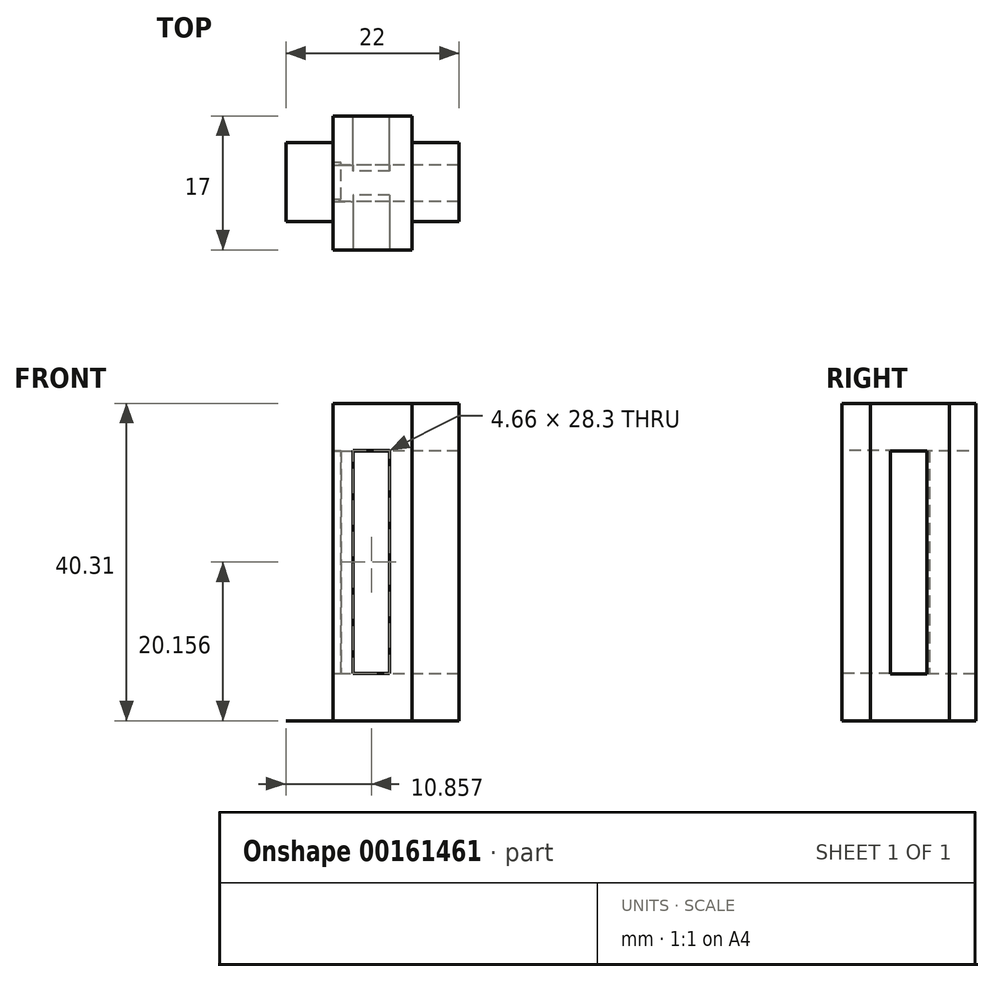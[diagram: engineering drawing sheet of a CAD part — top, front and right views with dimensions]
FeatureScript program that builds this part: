
annotation { "Feature Type Name" : "Feature", "Feature Type Description" : "" }
export const myFeature = defineFeature(function(context is Context, id is Id, definition is map)
    precondition{}
    {
        {
            var Q0;
            Q0=qCreatedBy(makeId("Front.planeOp"),FACE);
            var sketch = newSketch(context, id + "F0", { "sketchPlane" : qUnion([Q0])});
            skLineSegment(sketch, "E0.bottom", {"start": v(-30.25, -40.58) * mm, "end": v(-20.25, -40.58) * mm});
            skLineSegment(sketch, "E0.top", {"start": v(-30.25, -80.88) * mm, "end": v(-20.25, -80.88) * mm});
            skLineSegment(sketch, "E0.left", {"start": v(-30.25, -40.58) * mm, "end": v(-30.25, -80.88) * mm});
            skLineSegment(sketch, "E0.right", {"start": v(-20.25, -40.58) * mm, "end": v(-20.25, -80.88) * mm});
            skLineSegment(sketch, "E1.bottom", {"start": v(-23.06, -46.58) * mm, "end": v(-27.72, -46.58) * mm});
            skLineSegment(sketch, "E1.top", {"start": v(-23.06, -74.88) * mm, "end": v(-27.72, -74.88) * mm});
            skLineSegment(sketch, "E1.left", {"start": v(-23.06, -46.58) * mm, "end": v(-23.06, -74.88) * mm});
            skLineSegment(sketch, "E1.right", {"start": v(-27.72, -46.58) * mm, "end": v(-27.72, -74.88) * mm});
            skLineSegment(sketch, "E2", {"start": v(-23.06, -74.88) * mm, "end": v(-23.06, -80.88) * mm, "construction": true});
            skLineSegment(sketch, "E3", {"start": v(-27.72, -46.58) * mm, "end": v(-27.72, -40.58) * mm, "construction": true});
            skSolve(sketch);
        }
        {
            var Q0;
            Q0=makeQuery(id+"F0.imprint","IMPRINT",FACE,{"disambiguationData":[TD([[makeQuery(id+"F0.imprint","IMPRINT",EDGE,{"derivedFrom":sQuery(id+"F0.wireOp",EDGE,"E0.bottom")}),-1.0]])]});
            var Q1;
            Q1=makeQuery(id+"F0.imprint","IMPRINT",FACE,{"disambiguationData":[TD([[makeQuery(id+"F0.imprint","IMPRINT",EDGE,{"derivedFrom":sQuery(id+"F0.wireOp",EDGE,"0H4b4fvO-dyxi-FZrW-pJNc-f5h2Ua2qFgm1.bottom")}),-1.0]])]});
            var Q2;
            Q2=makeQuery(id+"F0.imprint","IMPRINT",FACE,{"disambiguationData":[TD([[makeQuery(id+"F0.imprint","IMPRINT",EDGE,{"derivedFrom":sQuery(id+"F0.wireOp",EDGE,"RIwqPRcQ-8Yhb-SA2c-7hZh-BoyqNhFDoh6P.bottom")}),-1.0]])]});
            var Q3;
            Q3=makeQuery(id+"F0.imprint","IMPRINT",FACE,{"disambiguationData":[TD([[makeQuery(id+"F0.imprint","IMPRINT",EDGE,{"derivedFrom":sQuery(id+"F0.wireOp",EDGE,"V1CP0RN2-3pWF-4ICx-AOtc-XG8nw0NRMOAc.bottom")}),-1.0]])]});
            var Q4;
            Q4=makeQuery(id+"F0.imprint","IMPRINT",FACE,{"disambiguationData":[TD([[makeQuery(id+"F0.imprint","IMPRINT",EDGE,{"derivedFrom":sQuery(id+"F0.wireOp",EDGE,"E1.bottom")}),1.0]])]});
            extrude(context, id + "F1", {"entities" : qUnion([Q0, Q1, Q2, Q3, Q4]), "depth" : 8.5 * mm});
        }
        {
            var Q0;
            Q0=makeQuery(id+"F0.imprint","IMPRINT",FACE,{"disambiguationData":[TD([[makeQuery(id+"F0.imprint","IMPRINT",EDGE,{"derivedFrom":sQuery(id+"F0.wireOp",EDGE,"0H4b4fvO-dyxi-FZrW-pJNc-f5h2Ua2qFgm1.bottom")}),-1.0]])]});
            var Q1;
            Q1=makeQuery(id+"F0.imprint","IMPRINT",FACE,{"disambiguationData":[TD([[makeQuery(id+"F0.imprint","IMPRINT",EDGE,{"derivedFrom":sQuery(id+"F0.wireOp",EDGE,"RIwqPRcQ-8Yhb-SA2c-7hZh-BoyqNhFDoh6P.bottom")}),-1.0]])]});
            var Q2;
            Q2=makeQuery(id+"F0.imprint","IMPRINT",FACE,{"disambiguationData":[TD([[makeQuery(id+"F0.imprint","IMPRINT",EDGE,{"derivedFrom":sQuery(id+"F0.wireOp",EDGE,"V1CP0RN2-3pWF-4ICx-AOtc-XG8nw0NRMOAc.bottom")}),-1.0]])]});
            var Q3;
            Q3=makeQuery(id+"F0.imprint","IMPRINT",FACE,{"disambiguationData":[TD([[makeQuery(id+"F0.imprint","IMPRINT",EDGE,{"derivedFrom":sQuery(id+"F0.wireOp",EDGE,"E1.bottom")}),1.0]])]});
            extrude(context, id + "F2", {"entities" : qUnion([Q0, Q1, Q2, Q3]), "operationType" : NewBodyOperationType.REMOVE, "depth" : 7 * mm});
        }
        {
            var Q0;
            Q0=makeQuery(id+"F1.opExtrude","SWEPT_BODY",BODY,{"disambiguationData":[OSD([sQuery(id+"F0.wireOp",EDGE,"E0.bottom"),sQuery(id+"F0.wireOp",EDGE,"E0.top"),sQuery(id+"F0.wireOp",EDGE,"E0.left"),sQuery(id+"F0.wireOp",EDGE,"E0.right")])]});
            var Q1;
            Q1=makeQuery(id+"F1.opExtrude","CAP_FACE",FACE,{"disambiguationData":[OSD([sQuery(id+"F0.wireOp",EDGE,"E0.bottom"),sQuery(id+"F0.wireOp",EDGE,"E0.top"),sQuery(id+"F0.wireOp",EDGE,"E0.left"),sQuery(id+"F0.wireOp",EDGE,"E0.right")])],"isStart":false});
            mirror(context, id + "F3", {"operationType" : NewBodyOperationType.ADD, "entities" : qUnion([Q0]), "mirrorPlane" : qUnion([Q1])});
        }
        {
            var Q0;
            Q0=makeQuery(id+"F3.opPattern","COPY",FACE,{"derivedFrom":makeQuery(id+"F1.opExtrude","SWEPT_FACE",FACE,{"disambiguationData":[OSD([sQuery(id+"F0.wireOp",EDGE,"E0.left")])]}),"instanceName":"1"});
            var sketch = newSketch(context, id + "F4", { "sketchPlane" : qUnion([Q0])});
            skLineSegment(sketch, "E4.bottom", {"start": v(3.37, -40.59) * mm, "end": v(13.37, -40.59) * mm});
            skLineSegment(sketch, "E4.top", {"start": v(3.37, -80.89) * mm, "end": v(13.37, -80.89) * mm});
            skLineSegment(sketch, "E4.left", {"start": v(3.37, -40.59) * mm, "end": v(3.37, -80.89) * mm});
            skLineSegment(sketch, "E4.right", {"start": v(13.37, -40.59) * mm, "end": v(13.37, -80.89) * mm});
            skLineSegment(sketch, "E5.bottom", {"start": v(10.56, -46.59) * mm, "end": v(5.9, -46.59) * mm});
            skLineSegment(sketch, "E5.top", {"start": v(10.56, -74.89) * mm, "end": v(5.9, -74.89) * mm});
            skLineSegment(sketch, "E5.left", {"start": v(10.56, -46.59) * mm, "end": v(10.56, -74.89) * mm});
            skLineSegment(sketch, "E5.right", {"start": v(5.9, -46.59) * mm, "end": v(5.9, -74.89) * mm});
            skLineSegment(sketch, "E6", {"start": v(10.56, -74.89) * mm, "end": v(10.56, -80.89) * mm, "construction": true});
            skLineSegment(sketch, "E7", {"start": v(5.9, -46.59) * mm, "end": v(5.9, -40.59) * mm, "construction": true});
            skSolve(sketch);
        }
        {
            var Q0;
            {var subQ1=sQuery(id+"F4.wireOp",EDGE,"E4.top");Q0=makeQuery(id+"F4.imprint","IMPRINT",FACE,{"disambiguationData":[TD([[makeQuery(id+"F4.imprint","IMPRINT",EDGE,{"derivedFrom":subQ1}),1.0]])]});}
            extrude(context, id + "F5", {"entities" : qUnion([Q0]), "operationType" : NewBodyOperationType.ADD, "depth" : 6 * mm});
        }
        {
            var Q0;
            Q0=makeQuery(id+"F4.imprint","IMPRINT",FACE,{"disambiguationData":[TD([[makeQuery(id+"F4.imprint","IMPRINT",EDGE,{"derivedFrom":sQuery(id+"F4.wireOp",EDGE,"E5.bottom")}),1.0]])]});
            extrude(context, id + "F6", {"entities" : qUnion([Q0]), "operationType" : NewBodyOperationType.REMOVE, "oppositeDirection" : true, "depth" : 1 * mm});
        }
        {
            var Q0;
            {var subQ0=makeQuery(id+"F1.opExtrude","SWEPT_FACE",FACE,{"disambiguationData":[OSD([sQuery(id+"F0.wireOp",EDGE,"E0.right")])]});Q0=makeQuery(id+"F3.boolean.opBoolean","MERGE",FACE,{"derivedFrom":[subQ0,makeQuery(id+"F3.opPattern","COPY",FACE,{"derivedFrom":subQ0,"instanceName":"1"})]});}
            var sketch = newSketch(context, id + "F7", { "sketchPlane" : qUnion([Q0])});
            skLineSegment(sketch, "E8.bottom", {"start": v(-13.39, -40.6) * mm, "end": v(-3.39, -40.6) * mm});
            skLineSegment(sketch, "E8.top", {"start": v(-13.39, -80.9) * mm, "end": v(-3.39, -80.9) * mm});
            skLineSegment(sketch, "E8.left", {"start": v(-13.39, -40.6) * mm, "end": v(-13.39, -80.9) * mm});
            skLineSegment(sketch, "E8.right", {"start": v(-3.39, -40.6) * mm, "end": v(-3.39, -80.9) * mm});
            skLineSegment(sketch, "E9.bottom", {"start": v(-6.2, -46.6) * mm, "end": v(-10.85, -46.6) * mm});
            skLineSegment(sketch, "E9.top", {"start": v(-6.2, -74.9) * mm, "end": v(-10.85, -74.9) * mm});
            skLineSegment(sketch, "E9.left", {"start": v(-6.2, -46.6) * mm, "end": v(-6.2, -74.9) * mm});
            skLineSegment(sketch, "E9.right", {"start": v(-10.85, -46.6) * mm, "end": v(-10.85, -74.9) * mm});
            skLineSegment(sketch, "E10", {"start": v(-6.2, -74.9) * mm, "end": v(-6.2, -80.9) * mm, "construction": true});
            skLineSegment(sketch, "E11", {"start": v(-10.85, -46.6) * mm, "end": v(-10.85, -40.6) * mm, "construction": true});
            skSolve(sketch);
        }
        {
            var Q0;
            {var subQ1=sQuery(id+"F7.wireOp",EDGE,"E8.bottom");Q0=makeQuery(id+"F7.imprint","IMPRINT",FACE,{"disambiguationData":[TD([[makeQuery(id+"F7.imprint","IMPRINT",EDGE,{"derivedFrom":subQ1}),-1.0]])]});}
            extrude(context, id + "F8", {"entities" : qUnion([Q0]), "operationType" : NewBodyOperationType.ADD, "depth" : 6 * mm});
        }
        {
            var Q0;
            {var subQ0=makeQuery(id+"F1.opExtrude","SWEPT_FACE",FACE,{"disambiguationData":[OSD([sQuery(id+"F0.wireOp",EDGE,"E0.right")])]});Q0=makeQuery(id+"F8.boolean.opBoolean","SPLIT",FACE,{"disambiguationData":[TD([makeQuery(id+"F8.opExtrude","SWEPT_FACE",FACE,{"disambiguationData":[OSD([sQuery(id+"F7.wireOp",EDGE,"E9.bottom")])]})])],"derivedFrom":makeQuery(id+"F3.boolean.opBoolean","MERGE",FACE,{"derivedFrom":[subQ0,makeQuery(id+"F3.opPattern","COPY",FACE,{"derivedFrom":subQ0,"instanceName":"1"})]})});}
            extrude(context, id + "F9", {"entities" : qUnion([Q0]), "operationType" : NewBodyOperationType.REMOVE, "oppositeDirection" : true, "depth" : 25.4 * mm});
        }
    });
